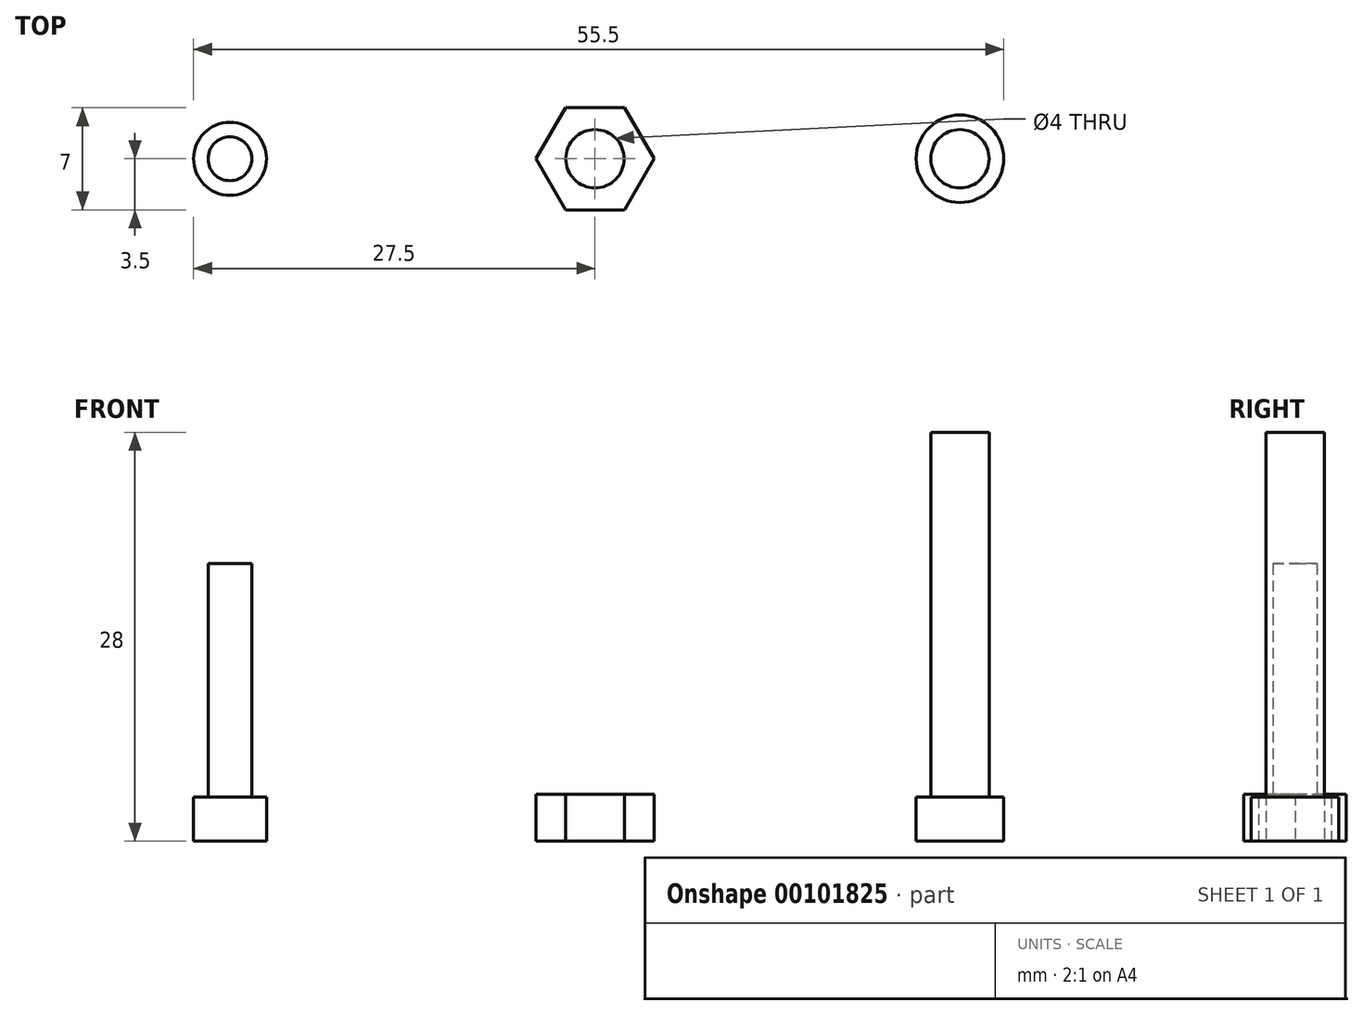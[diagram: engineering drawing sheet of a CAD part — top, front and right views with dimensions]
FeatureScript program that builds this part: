
annotation { "Feature Type Name" : "Feature", "Feature Type Description" : "" }
export const myFeature = defineFeature(function(context is Context, id is Id, definition is map)
    precondition{}
    {
        {
            var Q0;
            Q0=qCreatedBy(makeId("Top.planeOp"),FACE);
            var sketch = newSketch(context, id + "F0", { "sketchPlane" : qUnion([Q0])});
            skPoint(sketch, "E0", {"position": v(-25, 0) * mm});
            skPoint(sketch, "E1", {"position": v(25, 0) * mm});
            skCircle(sketch, "E2", {"center": v(-25, 0) * mm, "radius": 2.5 * mm});
            skCircle(sketch, "E3", {"center": v(25, 0) * mm, "radius": 3 * mm});
            skSolve(sketch);
        }
        {
            var Q0;
            Q0=makeQuery(id+"F0.imprint","IMPRINT",FACE,{"disambiguationData":[TD([[makeQuery(id+"F0.imprint","IMPRINT",EDGE,{"derivedFrom":sQuery(id+"F0.wireOp",EDGE,"E2")}),1.0]])]});
            extrude(context, id + "F1", {"entities" : qUnion([Q0]), "depth" : 3 * mm});
        }
        {
            var Q0;
            Q0=makeQuery(id+"F0.imprint","IMPRINT",FACE,{"disambiguationData":[TD([[makeQuery(id+"F0.imprint","IMPRINT",EDGE,{"derivedFrom":sQuery(id+"F0.wireOp",EDGE,"E3")}),1.0]])]});
            extrude(context, id + "F2", {"entities" : qUnion([Q0]), "depth" : 3 * mm});
        }
        {
            var Q0;
            Q0=makeQuery(id+"F1.opExtrude","CAP_FACE",FACE,{"disambiguationData":[OSD([sQuery(id+"F0.wireOp",EDGE,"E2")])],"isStart":false});
            var sketch = newSketch(context, id + "F3", { "sketchPlane" : qUnion([Q0])});
            skCircle(sketch, "E4", {"center": v(-25, 0) * mm, "radius": 1.5 * mm});
            skSolve(sketch);
        }
        {
            var Q0;
            Q0=makeQuery(id+"F3.imprint","IMPRINT",FACE,{"disambiguationData":[TD([[makeQuery(id+"F3.imprint","IMPRINT",EDGE,{"derivedFrom":sQuery(id+"F3.wireOp",EDGE,"E4")}),1.0]])]});
            extrude(context, id + "F4", {"entities" : qUnion([Q0]), "operationType" : NewBodyOperationType.ADD, "depth" : 16 * mm});
        }
        {
            var Q0;
            Q0=makeQuery(id+"F2.opExtrude","CAP_FACE",FACE,{"disambiguationData":[OSD([sQuery(id+"F0.wireOp",EDGE,"E3")])],"isStart":false});
            var sketch = newSketch(context, id + "F5", { "sketchPlane" : qUnion([Q0])});
            skCircle(sketch, "E5", {"center": v(25, 0) * mm, "radius": 2 * mm});
            skSolve(sketch);
        }
        {
            var Q0;
            Q0=makeQuery(id+"F5.imprint","IMPRINT",FACE,{"disambiguationData":[TD([[makeQuery(id+"F5.imprint","IMPRINT",EDGE,{"derivedFrom":sQuery(id+"F5.wireOp",EDGE,"E5")}),1.0]])]});
            extrude(context, id + "F6", {"entities" : qUnion([Q0]), "operationType" : NewBodyOperationType.ADD, "depth" : 25 * mm});
        }
        {
            var Q0;
            Q0=qCreatedBy(makeId("Top.planeOp"),FACE);
            var sketch = newSketch(context, id + "F7", { "sketchPlane" : qUnion([Q0])});
            skCircle(sketch, "E6.cCircle", {"center": v(0, 0) * mm, "radius": 3.5 * mm, "construction": true});
            skLineSegment(sketch, "E6.0", {"start": v(-2.02, 3.5) * mm, "end": v(2.02, 3.5) * mm});
            skLineSegment(sketch, "E6.1", {"start": v(2.02, 3.5) * mm, "end": v(4.04, 0) * mm});
            skLineSegment(sketch, "E6.2", {"start": v(4.04, 0) * mm, "end": v(2.02, -3.5) * mm});
            skLineSegment(sketch, "E6.3", {"start": v(2.02, -3.5) * mm, "end": v(-2.02, -3.5) * mm});
            skLineSegment(sketch, "E6.4", {"start": v(-2.02, -3.5) * mm, "end": v(-4.04, 0) * mm});
            skLineSegment(sketch, "E6.5", {"start": v(-4.04, 0) * mm, "end": v(-2.02, 3.5) * mm});
            skPoint(sketch, "E6.0.midPoint", {"position": v(0, 3.5) * mm});
            skCircle(sketch, "E7", {"center": v(0, 0) * mm, "radius": 2 * mm});
            skSolve(sketch);
        }
        {
            var Q0;
            Q0 = qSketchRegion(id + "F7", true);
            extrude(context, id + "F8", {"entities" : qUnion([Q0]), "depth" : 3.2 * mm});
        }
    });
